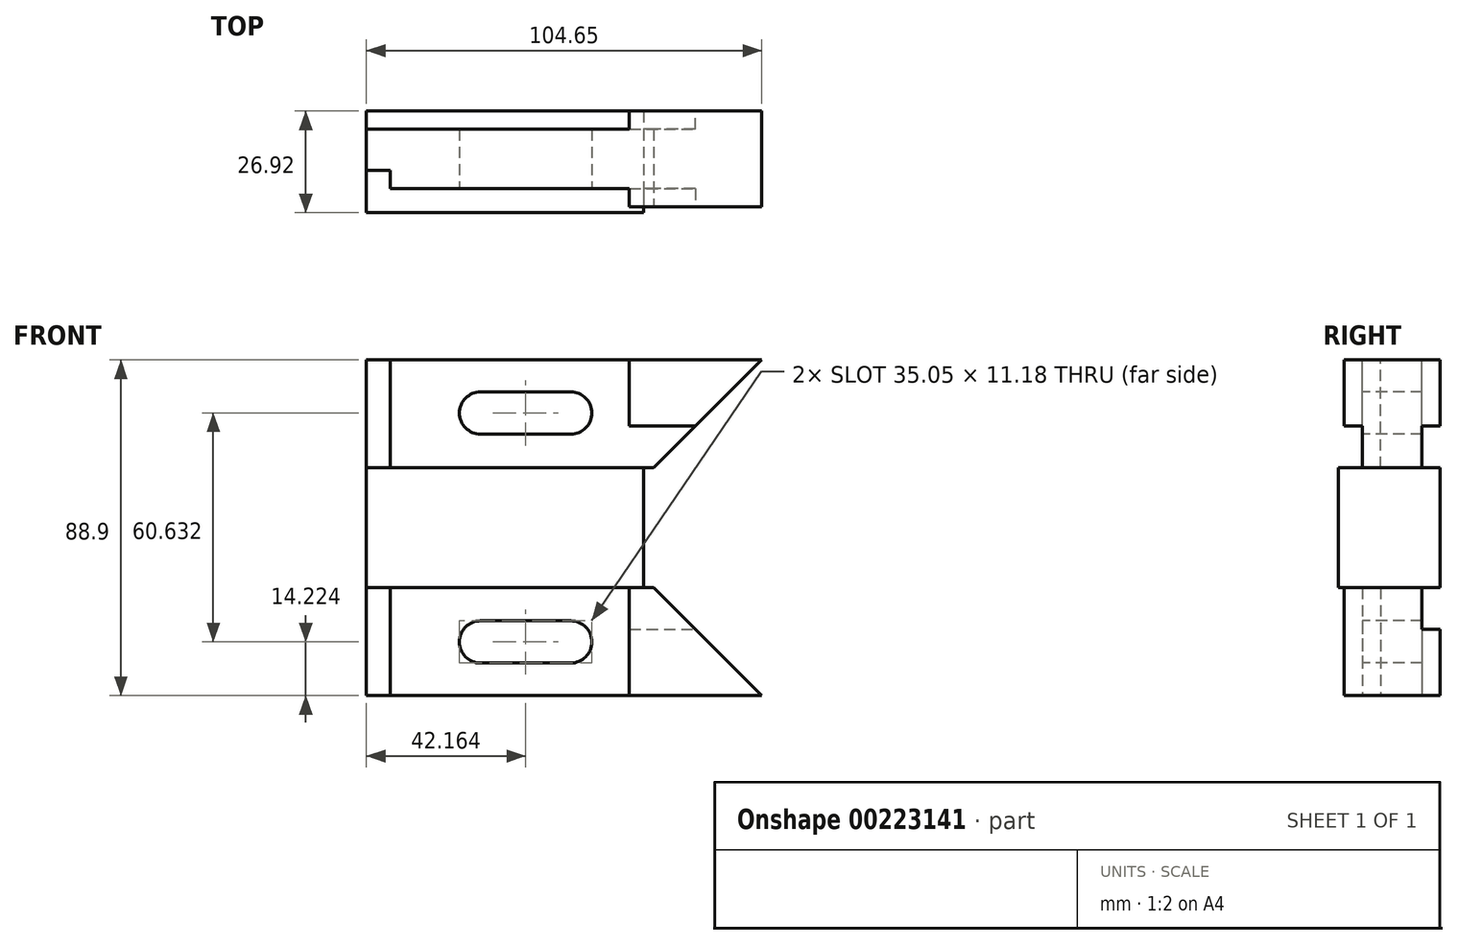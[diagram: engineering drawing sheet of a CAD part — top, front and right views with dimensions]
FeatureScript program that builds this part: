
annotation { "Feature Type Name" : "Feature", "Feature Type Description" : "" }
export const myFeature = defineFeature(function(context is Context, id is Id, definition is map)
    precondition{}
    {
        {
            var Q0;
            Q0=qCreatedBy(makeId("Right.planeOp"),FACE);
            var sketch = newSketch(context, id + "F0", { "sketchPlane" : qUnion([Q0])});
            skLineSegment(sketch, "E0", {"start": v(0, 0) * mm, "end": v(25.4, 0) * mm});
            skLineSegment(sketch, "E1", {"start": v(25.4, 0) * mm, "end": v(25.4, 28.58) * mm});
            skLineSegment(sketch, "E2", {"start": v(0, 0) * mm, "end": v(0, 28.58) * mm});
            skLineSegment(sketch, "E3", {"start": v(25.4, 60.33) * mm, "end": v(25.4, 88.9) * mm});
            skLineSegment(sketch, "E4", {"start": v(0, 60.33) * mm, "end": v(0, 88.9) * mm});
            skLineSegment(sketch, "E5", {"start": v(0, 88.9) * mm, "end": v(25.4, 88.9) * mm});
            skLineSegment(sketch, "E6", {"start": v(0, 28.58) * mm, "end": v(-1.52, 28.58) * mm});
            skLineSegment(sketch, "E7", {"start": v(-1.52, 28.58) * mm, "end": v(-1.52, 60.33) * mm});
            skLineSegment(sketch, "E8", {"start": v(0, 60.33) * mm, "end": v(-1.52, 60.33) * mm});
            skLineSegment(sketch, "E9", {"start": v(25.4, 60.33) * mm, "end": v(26.92, 60.33) * mm});
            skLineSegment(sketch, "E10", {"start": v(25.4, 28.58) * mm, "end": v(26.92, 28.58) * mm});
            skLineSegment(sketch, "E11", {"start": v(26.92, 60.33) * mm, "end": v(26.92, 28.58) * mm});
            skSolve(sketch);
        }
        {
            var Q0;
            Q0 = qSketchRegion(id + "F0", true);
            extrude(context, id + "F1", {"entities" : qUnion([Q0]), "depth" : 104.65 * mm});
        }
        {
            var Q0;
            Q0=makeQuery(id+"F1.opExtrude","SWEPT_FACE",FACE,{"disambiguationData":[OSD([sQuery(id+"F0.wireOp",EDGE,"E5")])]});
            var sketch = newSketch(context, id + "F2", { "sketchPlane" : qUnion([Q0])});
            skLineSegment(sketch, "E12.0.0", {"start": v(0, 0) * mm, "end": v(0, -1.52) * mm});
            skLineSegment(sketch, "E12.0.1", {"start": v(0, -1.52) * mm, "end": v(104.65, -1.52) * mm});
            skLineSegment(sketch, "E12.0.2", {"start": v(104.65, -1.52) * mm, "end": v(104.65, 0) * mm});
            skLineSegment(sketch, "E12.0.3", {"start": v(104.65, 0) * mm, "end": v(0, 0) * mm});
            skLineSegment(sketch, "E13", {"start": v(0, -1.52) * mm, "end": v(0, 4.83) * mm});
            skLineSegment(sketch, "E14.0.0", {"start": v(0, 26.92) * mm, "end": v(0, 25.4) * mm});
            skLineSegment(sketch, "E14.0.1", {"start": v(0, 25.4) * mm, "end": v(104.65, 25.4) * mm});
            skLineSegment(sketch, "E14.0.2", {"start": v(104.65, 25.4) * mm, "end": v(104.65, 26.92) * mm});
            skLineSegment(sketch, "E14.0.3", {"start": v(104.65, 26.92) * mm, "end": v(0, 26.92) * mm});
            skLineSegment(sketch, "E15", {"start": v(0, 26.92) * mm, "end": v(0, 20.57) * mm});
            skLineSegment(sketch, "E16", {"start": v(0, 4.83) * mm, "end": v(0, 9.65) * mm});
            skLineSegment(sketch, "E17", {"start": v(0, 9.65) * mm, "end": v(6.35, 9.65) * mm});
            skLineSegment(sketch, "E18", {"start": v(6.35, 9.65) * mm, "end": v(6.35, 4.83) * mm});
            skLineSegment(sketch, "E19", {"start": v(6.35, 4.83) * mm, "end": v(69.6, 4.83) * mm});
            skLineSegment(sketch, "E20", {"start": v(0, 20.57) * mm, "end": v(69.6, 20.57) * mm});
            skLineSegment(sketch, "E21", {"start": v(69.6, 20.57) * mm, "end": v(69.6, 25.4) * mm});
            skLineSegment(sketch, "E22", {"start": v(69.6, 4.83) * mm, "end": v(69.6, 0) * mm});
            skLineSegment(sketch, "E23", {"start": v(0, -1.52) * mm, "end": v(73.4, -1.52) * mm});
            skLineSegment(sketch, "E24", {"start": v(73.4, -1.52) * mm, "end": v(73.4, 0) * mm});
            skLineSegment(sketch, "E25", {"start": v(73.4, 0) * mm, "end": v(0, 0) * mm});
            skLineSegment(sketch, "E26", {"start": v(0, 25.4) * mm, "end": v(0, 26.92) * mm});
            skLineSegment(sketch, "E27", {"start": v(0, 26.92) * mm, "end": v(73.4, 26.92) * mm});
            skLineSegment(sketch, "E28", {"start": v(73.4, 26.92) * mm, "end": v(73.4, 25.4) * mm});
            skLineSegment(sketch, "E29", {"start": v(73.4, 25.4) * mm, "end": v(0, 25.4) * mm});
            skSolve(sketch);
        }
        {
            var Q0;
            {var subQ0=sQuery(id+"F2.wireOp",EDGE,"E15");Q0=makeQuery(id+"F2.imprint","IMPRINT",FACE,{"disambiguationData":[TD([[makeQuery(id+"F2.imprint","IMPRINT",EDGE,{"derivedFrom":subQ0}),-1.0]])]});}
            var Q1;
            {var subQ0=sQuery(id+"F2.wireOp",EDGE,"E16");Q1=makeQuery(id+"F2.imprint","IMPRINT",FACE,{"disambiguationData":[TD([[makeQuery(id+"F2.imprint","IMPRINT",EDGE,{"derivedFrom":subQ0}),-1.0]])]});}
            extrude(context, id + "F3", {"entities" : qUnion([Q0, Q1]), "operationType" : NewBodyOperationType.REMOVE, "oppositeDirection" : true, "depth" : 28.57 * mm});
        }
        {
            var Q0;
            Q0=makeQuery(id+"F2.imprint","IMPRINT",FACE,{"disambiguationData":[TD([[makeQuery(id+"F2.imprint","IMPRINT",EDGE,{"derivedFrom":sQuery(id+"F2.wireOp",EDGE,"E14.0.1")}),-1.0]])]});
            var Q1;
            Q1=makeQuery(id+"F2.imprint","IMPRINT",FACE,{"disambiguationData":[TD([[makeQuery(id+"F2.imprint","IMPRINT",EDGE,{"derivedFrom":sQuery(id+"F2.wireOp",EDGE,"E12.0.1")}),1.0]])]});
            extrude(context, id + "F4", {"entities" : qUnion([Q0, Q1]), "operationType" : NewBodyOperationType.REMOVE, "oppositeDirection" : true, "depth" : 88.9 * mm});
        }
        {
            var Q0;
            Q0=makeQuery(id+"F1.opExtrude","SWEPT_FACE",FACE,{"disambiguationData":[OSD([sQuery(id+"F0.wireOp",EDGE,"E0")])]});
            var sketch = newSketch(context, id + "F5", { "sketchPlane" : qUnion([Q0])});
            skLineSegment(sketch, "E30.0", {"start": v(6.35, -4.83) * mm, "end": v(69.6, -4.83) * mm});
            skPoint(sketch, "E31.0", {"position": v(6.35, -9.65) * mm});
            skPoint(sketch, "E32.0", {"position": v(3.18, -9.65) * mm});
            skLineSegment(sketch, "E33.0", {"start": v(0, -9.65) * mm, "end": v(0, -20.57) * mm});
            skLineSegment(sketch, "E34.0", {"start": v(0, -20.57) * mm, "end": v(69.6, -20.57) * mm});
            skLineSegment(sketch, "E35.0", {"start": v(104.65, -25.4) * mm, "end": v(69.6, -25.4) * mm});
            skPoint(sketch, "E36.0", {"position": v(69.6, -22.99) * mm});
            skLineSegment(sketch, "E37.0", {"start": v(104.65, 0) * mm, "end": v(69.6, 0) * mm});
            skLineSegment(sketch, "E38.0", {"start": v(69.6, -4.83) * mm, "end": v(69.6, 0) * mm});
            skLineSegment(sketch, "E39.0", {"start": v(69.6, -20.57) * mm, "end": v(69.6, -25.4) * mm});
            skLineSegment(sketch, "E40.0.0", {"start": v(73.4, -25.4) * mm, "end": v(73.4, -26.92) * mm});
            skLineSegment(sketch, "E40.0.1", {"start": v(73.4, -26.92) * mm, "end": v(0, -26.92) * mm});
            skLineSegment(sketch, "E40.0.2", {"start": v(0, -26.92) * mm, "end": v(0, -20.57) * mm});
            skLineSegment(sketch, "E40.0.5", {"start": v(69.6, -25.4) * mm, "end": v(73.4, -25.4) * mm});
            skLineSegment(sketch, "E41.0.0", {"start": v(73.4, 1.52) * mm, "end": v(73.4, 0) * mm});
            skLineSegment(sketch, "E41.0.1", {"start": v(73.4, 0) * mm, "end": v(69.6, 0) * mm});
            skLineSegment(sketch, "E41.0.2", {"start": v(69.6, 0) * mm, "end": v(69.6, -4.83) * mm});
            skLineSegment(sketch, "E41.0.3", {"start": v(69.6, -4.83) * mm, "end": v(6.35, -4.83) * mm});
            skLineSegment(sketch, "E41.0.4", {"start": v(6.35, -4.83) * mm, "end": v(6.35, -9.65) * mm});
            skLineSegment(sketch, "E41.0.5", {"start": v(6.35, -9.65) * mm, "end": v(0, -9.65) * mm});
            skLineSegment(sketch, "E41.0.6", {"start": v(0, -9.65) * mm, "end": v(0, 1.52) * mm});
            skLineSegment(sketch, "E41.0.7", {"start": v(0, 1.52) * mm, "end": v(73.4, 1.52) * mm});
            skSolve(sketch);
        }
        {
            var Q0;
            Q0 = qSketchRegion(id + "F5", true);
            extrude(context, id + "F6", {"entities" : qUnion([Q0]), "operationType" : NewBodyOperationType.REMOVE, "oppositeDirection" : true, "depth" : 28.57 * mm});
        }
        {
            var Q0;
            Q0=makeQuery(id+"F4.boolean.opBoolean","MERGE",FACE,{"derivedFrom":[makeQuery(id+"F1.opExtrude","SWEPT_FACE",FACE,{"disambiguationData":[OSD([sQuery(id+"F0.wireOp",EDGE,"E2")])]}),makeQuery(id+"F1.opExtrude","SWEPT_FACE",FACE,{"disambiguationData":[OSD([sQuery(id+"F0.wireOp",EDGE,"E4")])]}),makeQuery(id+"F4.opExtrude","SWEPT_FACE",FACE,{"disambiguationData":[OSD([sQuery(id+"F2.wireOp",EDGE,"E12.0.3")])]})]});
            var sketch = newSketch(context, id + "F7", { "sketchPlane" : qUnion([Q0])});
            skLineSegment(sketch, "E42.0", {"start": v(104.65, 88.9) * mm, "end": v(69.6, 88.9) * mm});
            skLineSegment(sketch, "E43.0", {"start": v(69.6, 71.37) * mm, "end": v(69.6, 88.9) * mm});
            skLineSegment(sketch, "E44.0", {"start": v(6.35, 88.9) * mm, "end": v(69.6, 88.9) * mm});
            skLineSegment(sketch, "E45.0.0", {"start": v(69.6, 88.9) * mm, "end": v(6.35, 88.9) * mm});
            skLineSegment(sketch, "E45.0.1", {"start": v(6.35, 88.9) * mm, "end": v(6.35, 60.33) * mm});
            skLineSegment(sketch, "E45.0.2", {"start": v(6.35, 60.33) * mm, "end": v(69.6, 60.33) * mm});
            skLineSegment(sketch, "E46.0.0", {"start": v(0, 28.58) * mm, "end": v(73.4, 28.58) * mm});
            skLineSegment(sketch, "E46.0.1", {"start": v(73.4, 28.58) * mm, "end": v(73.4, 60.33) * mm});
            skLineSegment(sketch, "E46.0.2", {"start": v(73.4, 60.33) * mm, "end": v(0, 60.33) * mm});
            skLineSegment(sketch, "E46.0.3", {"start": v(0, 60.33) * mm, "end": v(0, 28.58) * mm});
            skLineSegment(sketch, "E47.0.0", {"start": v(6.35, 0) * mm, "end": v(69.6, 0) * mm});
            skLineSegment(sketch, "E47.0.1", {"start": v(69.6, 0) * mm, "end": v(69.6, 28.58) * mm});
            skLineSegment(sketch, "E47.0.2", {"start": v(69.6, 28.58) * mm, "end": v(6.35, 28.58) * mm});
            skLineSegment(sketch, "E47.0.3", {"start": v(6.35, 28.58) * mm, "end": v(6.35, 0) * mm});
            skLineSegment(sketch, "E48.0.0", {"start": v(73.4, 60.33) * mm, "end": v(73.4, 28.58) * mm});
            skLineSegment(sketch, "E48.0.1", {"start": v(73.4, 28.58) * mm, "end": v(69.6, 28.58) * mm});
            skLineSegment(sketch, "E48.0.2", {"start": v(69.6, 28.58) * mm, "end": v(69.6, 0) * mm});
            skLineSegment(sketch, "E48.0.3", {"start": v(69.6, 0) * mm, "end": v(104.65, 0) * mm});
            skLineSegment(sketch, "E48.0.4", {"start": v(104.65, 0) * mm, "end": v(104.65, 88.9) * mm});
            skLineSegment(sketch, "E48.0.6", {"start": v(69.6, 88.9) * mm, "end": v(69.6, 60.33) * mm});
            skLineSegment(sketch, "E48.0.7", {"start": v(69.6, 60.33) * mm, "end": v(73.4, 60.33) * mm});
            skPoint(sketch, "E49.0", {"position": v(0, 14.29) * mm});
            skPoint(sketch, "E50.0", {"position": v(0, 74.61) * mm});
            skLineSegment(sketch, "E51.0", {"start": v(0, 60.33) * mm, "end": v(0, 88.9) * mm});
            skLineSegment(sketch, "E52.0", {"start": v(0, 88.9) * mm, "end": v(6.35, 88.9) * mm});
            skLineSegment(sketch, "E53", {"start": v(0, 88.9) * mm, "end": v(69.6, 88.9) * mm});
            skLineSegment(sketch, "E54", {"start": v(69.6, 88.9) * mm, "end": v(69.6, 71.37) * mm});
            skLineSegment(sketch, "E55", {"start": v(69.6, 71.37) * mm, "end": v(87.12, 71.37) * mm});
            skLineSegment(sketch, "E56", {"start": v(104.65, 88.9) * mm, "end": v(76.07, 60.33) * mm});
            skLineSegment(sketch, "E57", {"start": v(73.4, 60.33) * mm, "end": v(76.07, 60.33) * mm});
            skLineSegment(sketch, "E58", {"start": v(69.6, 0) * mm, "end": v(69.6, 14.29) * mm});
            skLineSegment(sketch, "E59", {"start": v(104.65, 44.45) * mm, "end": v(0, 44.45) * mm});
            skLineSegment(sketch, "E60.MirrorCS", {"start": v(104.65, 0) * mm, "end": v(76.07, 28.58) * mm});
            skLineSegment(sketch, "E61.MirrorCS", {"start": v(73.4, 28.58) * mm, "end": v(76.07, 28.58) * mm});
            skLineSegment(sketch, "E62.MirrorCS", {"start": v(69.6, 17.53) * mm, "end": v(87.12, 17.53) * mm});
            skSolve(sketch);
        }
        {
            var Q0;
            {var subQ5=sQuery(id+"F7.wireOp",EDGE,"E57");Q0=makeQuery(id+"F7.imprint","IMPRINT",FACE,{"disambiguationData":[TD([[makeQuery(id+"F7.imprint","IMPRINT",EDGE,{"derivedFrom":subQ5}),-1.0]])]});}
            var Q1;
            {var subQ8=sQuery(id+"F7.wireOp",EDGE,"E61.MirrorCS");Q1=makeQuery(id+"F7.imprint","IMPRINT",FACE,{"disambiguationData":[TD([[makeQuery(id+"F7.imprint","IMPRINT",EDGE,{"derivedFrom":subQ8}),1.0]])]});}
            extrude(context, id + "F8", {"entities" : qUnion([Q0, Q1]), "operationType" : NewBodyOperationType.REMOVE, "endBound" : BoundingType.THROUGH_ALL, "oppositeDirection" : true, "depth" : 25.4 * mm});
        }
        {
            var Q0;
            Q0=makeQuery(id+"F7.imprint","IMPRINT",FACE,{"disambiguationData":[TD([[makeQuery(id+"F7.imprint","IMPRINT",EDGE,{"derivedFrom":sQuery(id+"F7.wireOp",EDGE,"E48.0.6")}),-1.0]])]});
            var Q1;
            {var subQ1=sQuery(id+"F7.wireOp",EDGE,"E48.0.1");Q1=makeQuery(id+"F7.imprint","IMPRINT",FACE,{"disambiguationData":[TD([[makeQuery(id+"F7.imprint","IMPRINT",EDGE,{"derivedFrom":subQ1}),1.0]])]});}
            extrude(context, id + "F9", {"entities" : qUnion([Q0, Q1]), "operationType" : NewBodyOperationType.REMOVE, "oppositeDirection" : true, "depth" : 4.83 * mm});
        }
        {
            var Q0;
            Q0=makeQuery(id+"F8.boolean.opBoolean","SPLIT",FACE,{"disambiguationData":[TD([makeQuery(id+"F1.opExtrude","SWEPT_FACE",FACE,{"disambiguationData":[OSD([sQuery(id+"F0.wireOp",EDGE,"E0")])]})])],"derivedFrom":makeQuery(id+"F4.boolean.opBoolean","MERGE",FACE,{"derivedFrom":[makeQuery(id+"F1.opExtrude","SWEPT_FACE",FACE,{"disambiguationData":[OSD([sQuery(id+"F0.wireOp",EDGE,"E1")])]}),makeQuery(id+"F1.opExtrude","SWEPT_FACE",FACE,{"disambiguationData":[OSD([sQuery(id+"F0.wireOp",EDGE,"E3")])]}),makeQuery(id+"F4.opExtrude","SWEPT_FACE",FACE,{"disambiguationData":[OSD([sQuery(id+"F2.wireOp",EDGE,"E14.0.1")])]})]})});
            var sketch = newSketch(context, id + "F10", { "sketchPlane" : qUnion([Q0])});
            skLineSegment(sketch, "E63.0", {"start": v(-69.6, 71.37) * mm, "end": v(-87.12, 71.37) * mm});
            skLineSegment(sketch, "E64.0", {"start": v(-104.65, 88.9) * mm, "end": v(-76.07, 60.33) * mm});
            skLineSegment(sketch, "E65.0.0", {"start": v(-69.6, 60.33) * mm, "end": v(-73.4, 60.33) * mm});
            skLineSegment(sketch, "E65.0.1", {"start": v(-73.4, 60.33) * mm, "end": v(-76.07, 60.33) * mm});
            skLineSegment(sketch, "E65.0.2", {"start": v(-76.07, 60.33) * mm, "end": v(-87.12, 71.37) * mm});
            skLineSegment(sketch, "E65.0.3", {"start": v(-87.12, 71.37) * mm, "end": v(-69.6, 71.37) * mm});
            skLineSegment(sketch, "E65.0.4", {"start": v(-69.6, 71.37) * mm, "end": v(-69.6, 60.33) * mm});
            skLineSegment(sketch, "E66.0.0", {"start": v(-69.6, 28.58) * mm, "end": v(-69.6, 17.53) * mm});
            skLineSegment(sketch, "E66.0.1", {"start": v(-69.6, 17.53) * mm, "end": v(-87.12, 17.53) * mm});
            skLineSegment(sketch, "E66.0.2", {"start": v(-87.12, 17.53) * mm, "end": v(-76.07, 28.58) * mm});
            skLineSegment(sketch, "E66.0.3", {"start": v(-76.07, 28.58) * mm, "end": v(-73.4, 28.58) * mm});
            skLineSegment(sketch, "E66.0.4", {"start": v(-73.4, 28.58) * mm, "end": v(-69.6, 28.58) * mm});
            skSolve(sketch);
        }
        {
            var Q0;
            Q0 = qSketchRegion(id + "F10", true);
            extrude(context, id + "F11", {"entities" : qUnion([Q0]), "operationType" : NewBodyOperationType.REMOVE, "oppositeDirection" : true, "depth" : 4.83 * mm});
        }
        {
            var Q0;
            Q0=makeQuery(id+"F7.imprint","IMPRINT",FACE,{"disambiguationData":[TD([[makeQuery(id+"F7.imprint","IMPRINT",EDGE,{"derivedFrom":sQuery(id+"F7.wireOp",EDGE,"E47.0.0")}),1.0]])]});
            var sketch = newSketch(context, id + "F12", { "sketchPlane" : qUnion([Q0])});
            skLineSegment(sketch, "E67", {"start": v(0, 0) * mm, "end": v(0, 14.22) * mm});
            skLineSegment(sketch, "E68", {"start": v(0, 0) * mm, "end": v(24.64, 0) * mm});
            skLineSegment(sketch, "E69", {"start": v(24.64, 0) * mm, "end": v(24.64, 14.22) * mm});
            skLineSegment(sketch, "E70", {"start": v(24.64, 14.22) * mm, "end": v(59.69, 14.22) * mm});
            skLineSegment(sketch, "E71", {"start": v(24.64, 14.22) * mm, "end": v(30.23, 14.22) * mm});
            skCircle(sketch, "E72", {"center": v(30.23, 14.22) * mm, "radius": 5.59 * mm});
            skCircle(sketch, "E73", {"center": v(54.1, 14.22) * mm, "radius": 5.59 * mm});
            skLineSegment(sketch, "E74", {"start": v(30.23, 19.81) * mm, "end": v(54.1, 19.81) * mm});
            skLineSegment(sketch, "E75", {"start": v(30.23, 8.64) * mm, "end": v(54.1, 8.64) * mm});
            skLineSegment(sketch, "E76", {"start": v(0, 44.54) * mm, "end": v(88.44, 44.54) * mm});
            skCircle(sketch, "E77.MirrorC", {"center": v(54.1, 74.86) * mm, "radius": 5.59 * mm});
            skLineSegment(sketch, "E78.MirrorCS", {"start": v(24.64, 74.86) * mm, "end": v(59.69, 74.86) * mm});
            skCircle(sketch, "E79.MirrorC", {"center": v(30.23, 74.86) * mm, "radius": 5.59 * mm});
            skLineSegment(sketch, "E80.MirrorCS", {"start": v(30.23, 80.44) * mm, "end": v(54.1, 80.44) * mm});
            skLineSegment(sketch, "E81.MirrorCS", {"start": v(30.23, 69.27) * mm, "end": v(54.1, 69.27) * mm});
            skSolve(sketch);
        }
        {
            var Q0;
            Q0 = qSketchRegion(id + "F12", true);
            extrude(context, id + "F13", {"entities" : qUnion([Q0]), "operationType" : NewBodyOperationType.REMOVE, "endBound" : BoundingType.THROUGH_ALL, "oppositeDirection" : true, "depth" : 25.4 * mm});
        }
    });
